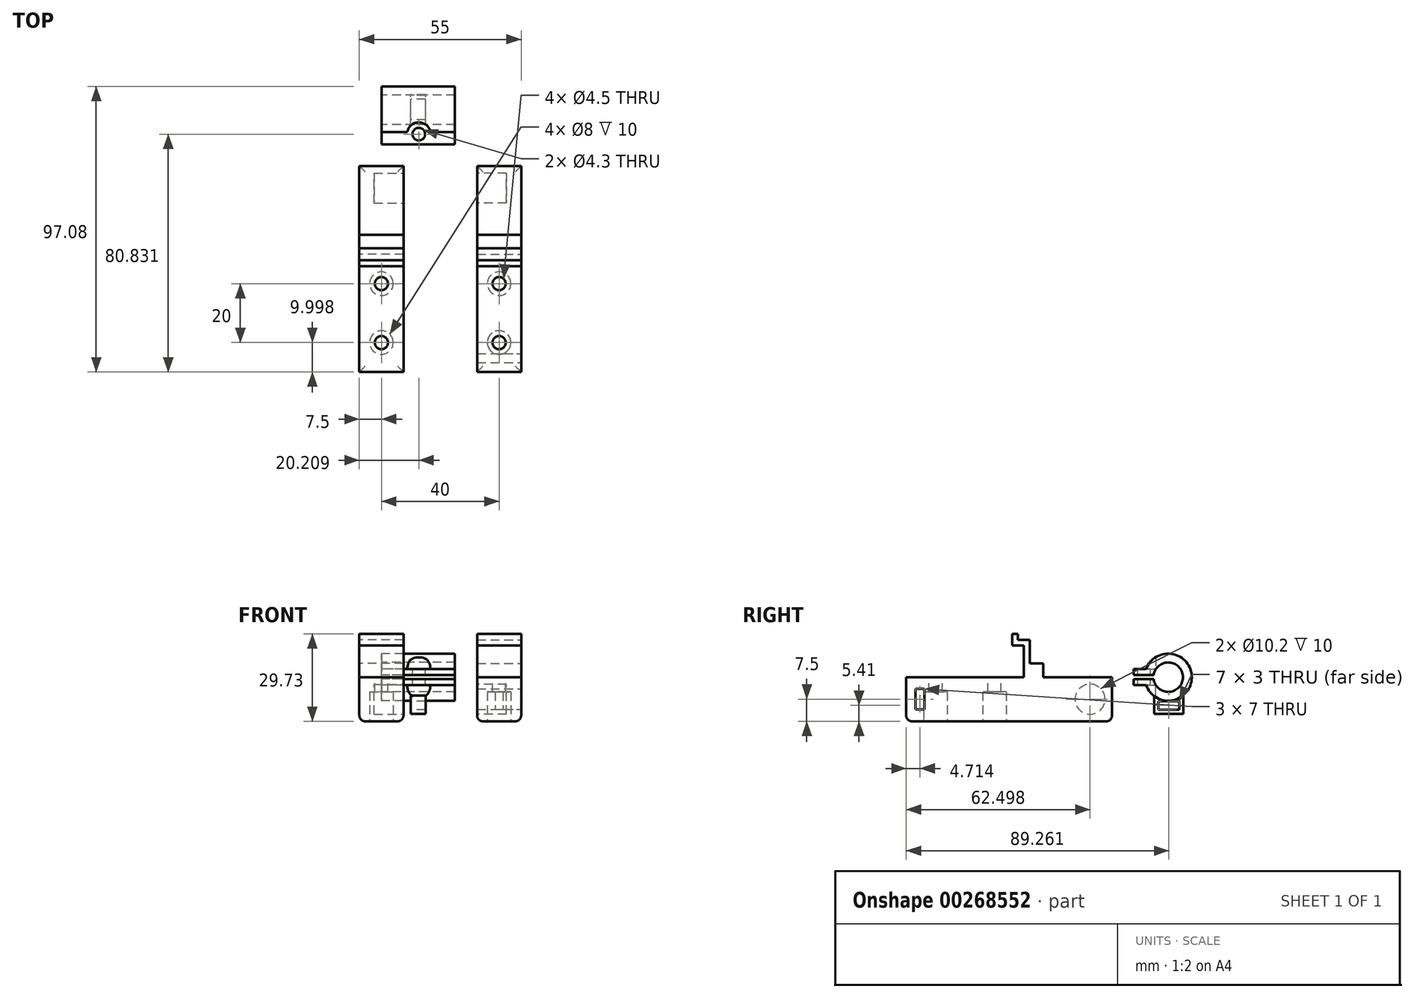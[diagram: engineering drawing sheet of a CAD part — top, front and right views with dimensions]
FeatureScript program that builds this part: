
annotation { "Feature Type Name" : "Feature", "Feature Type Description" : "" }
export const myFeature = defineFeature(function(context is Context, id is Id, definition is map)
    precondition{}
    {
        {
            var Q0;
            Q0=qCreatedBy(makeId("Top.planeOp"),FACE);
            var sketch = newSketch(context, id + "F0", { "sketchPlane" : qUnion([Q0])});
            skLineSegment(sketch, "E0", {"start": v(120.64, 20) * mm, "end": v(-98.83, 20) * mm, "construction": true});
            skLineSegment(sketch, "E1", {"start": v(-113.57, -20) * mm, "end": v(119.85, -20) * mm, "construction": true});
            skLineSegment(sketch, "E2", {"start": v(-15.81, 35.6) * mm, "end": v(120.22, 35.6) * mm, "construction": true});
            skLineSegment(sketch, "E3", {"start": v(0, 0) * mm, "end": v(121.2, 0) * mm, "construction": true});
            skSolve(sketch);
        }
        {
            var Q0;
            Q0=qCreatedBy(makeId("Right.planeOp"),FACE);
            var sketch = newSketch(context, id + "F1", { "sketchPlane" : qUnion([Q0])});
            skLineSegment(sketch, "E4", {"start": v(13.49, 0) * mm, "end": v(-26.51, 0) * mm});
            skLineSegment(sketch, "E5", {"start": v(-26.51, 0) * mm, "end": v(-26.51, -15) * mm});
            skLineSegment(sketch, "E6", {"start": v(-26.51, -15) * mm, "end": v(18.49, -15) * mm});
            skLineSegment(sketch, "E7", {"start": v(13.49, 10.73) * mm, "end": v(13.49, 0) * mm});
            skLineSegment(sketch, "E8", {"start": v(43.49, -15) * mm, "end": v(43.49, 0) * mm});
            skLineSegment(sketch, "E9", {"start": v(43.49, 0) * mm, "end": v(20.14, 0) * mm});
            skLineSegment(sketch, "E10", {"start": v(13.49, 10.73) * mm, "end": v(9.49, 10.73) * mm});
            skLineSegment(sketch, "E11", {"start": v(9.49, 10.73) * mm, "end": v(9.49, 14.73) * mm});
            skLineSegment(sketch, "E12", {"start": v(9.49, 14.73) * mm, "end": v(11.49, 14.73) * mm});
            skLineSegment(sketch, "E13", {"start": v(11.49, 14.73) * mm, "end": v(11.49, 12.73) * mm});
            skLineSegment(sketch, "E14", {"start": v(18.49, -15) * mm, "end": v(43.49, -15) * mm});
            skLineSegment(sketch, "E15", {"start": v(20.14, 0) * mm, "end": v(20.14, 4.7) * mm});
            skLineSegment(sketch, "E16", {"start": v(20.14, 4.7) * mm, "end": v(15.49, 4.7) * mm});
            skPoint(sketch, "E17.orphan", {"position": v(15.49, 0) * mm});
            skPoint(sketch, "E18.end.orphan", {"position": v(13.49, 21.47) * mm});
            skLineSegment(sketch, "E19", {"start": v(15.49, 4.7) * mm, "end": v(15.49, 12.7) * mm});
            skPoint(sketch, "E20.end.orphan", {"position": v(13.49, 12) * mm});
            skLineSegment(sketch, "E21", {"start": v(15.49, 12.7) * mm, "end": v(11.49, 12.73) * mm});
            skSolve(sketch);
        }
        {
            var Q0;
            Q0=makeQuery(id+"F1.imprint","IMPRINT",FACE,{"disambiguationData":[TD([[makeQuery(id+"F1.imprint","IMPRINT",EDGE,{"derivedFrom":sQuery(id+"F1.wireOp",EDGE,"E4")}),1.0]])]});
            var Q1;
            {var subQ0=sQuery(id+"F1.wireOp",EDGE,"E10");Q1=makeQuery(id+"F1.imprint","IMPRINT",FACE,{"disambiguationData":[TD([[makeQuery(id+"F1.imprint","IMPRINT",EDGE,{"derivedFrom":subQ0}),-1.0]])]});}
            extrude(context, id + "F2", {"entities" : qUnion([Q0, Q1]), "endBound" : BoundingType.SYMMETRIC, "depth" : 15 * mm});
        }
        {
            var Q0;
            Q0=makeQuery(id+"F2.opExtrude","CAP_FACE",FACE,{"disambiguationData":[OSD([sQuery(id+"F1.wireOp",EDGE,"E4"),sQuery(id+"F1.wireOp",EDGE,"E5"),sQuery(id+"F1.wireOp",EDGE,"E6"),sQuery(id+"F1.wireOp",EDGE,"E7"),sQuery(id+"F1.wireOp",EDGE,"E8"),sQuery(id+"F1.wireOp",EDGE,"E9"),sQuery(id+"F1.wireOp",EDGE,"E10"),sQuery(id+"F1.wireOp",EDGE,"E11"),sQuery(id+"F1.wireOp",EDGE,"E12"),sQuery(id+"F1.wireOp",EDGE,"E13"),sQuery(id+"F1.wireOp",EDGE,"E14"),sQuery(id+"F1.wireOp",EDGE,"E15"),sQuery(id+"F1.wireOp",EDGE,"E16"),sQuery(id+"F1.wireOp",EDGE,"E19"),sQuery(id+"F1.wireOp",EDGE,"E21")])],"isStart":false});
            var sketch = newSketch(context, id + "F3", { "sketchPlane" : qUnion([Q0])});
            skCircle(sketch, "E22", {"center": v(35.99, -7.5) * mm, "radius": 5.1 * mm});
            skSolve(sketch);
        }
        {
            var Q0;
            Q0=makeQuery(id+"F3.imprint","IMPRINT",FACE,{"disambiguationData":[TD([[makeQuery(id+"F3.imprint","IMPRINT",EDGE,{"derivedFrom":sQuery(id+"F3.wireOp",EDGE,"E22")}),1.0]])]});
            extrude(context, id + "F4", {"entities" : qUnion([Q0]), "operationType" : NewBodyOperationType.REMOVE, "oppositeDirection" : true, "depth" : 10 * mm});
        }
        {
            var Q0;
            Q0=qCreatedBy(makeId("Right.planeOp"),FACE);
            cPlane(context, id + "F5", {"entities" : qUnion([Q0]), "cplaneType" : CPlaneType.OFFSET, "offset" : 20 * mm, "width" : 150 * mm, "height" : 150 * mm});
        }
        {
            var Q0;
            Q0=makeQuery(id+"F2.opExtrude","SWEPT_BODY",BODY,{"disambiguationData":[OSD([sQuery(id+"F1.wireOp",EDGE,"E4"),sQuery(id+"F1.wireOp",EDGE,"E5"),sQuery(id+"F1.wireOp",EDGE,"E6"),sQuery(id+"F1.wireOp",EDGE,"E7"),sQuery(id+"F1.wireOp",EDGE,"E8"),sQuery(id+"F1.wireOp",EDGE,"E9"),sQuery(id+"F1.wireOp",EDGE,"E10"),sQuery(id+"F1.wireOp",EDGE,"E11"),sQuery(id+"F1.wireOp",EDGE,"E12"),sQuery(id+"F1.wireOp",EDGE,"E13"),sQuery(id+"F1.wireOp",EDGE,"E14"),sQuery(id+"F1.wireOp",EDGE,"E15"),sQuery(id+"F1.wireOp",EDGE,"E16"),sQuery(id+"F1.wireOp",EDGE,"E19"),sQuery(id+"F1.wireOp",EDGE,"E21")])]});
            var Q1;
            Q1=qCreatedBy(id+"F5.planeOp",FACE);
            mirror(context, id + "F6", {"entities" : qUnion([Q0]), "mirrorPlane" : qUnion([Q1])});
        }
        {
            var Q0;
            Q0=makeQuery(id+"F6.opPattern","COPY",FACE,{"derivedFrom":makeQuery(id+"F2.opExtrude","CAP_FACE",FACE,{"disambiguationData":[OSD([sQuery(id+"F1.wireOp",EDGE,"E4"),sQuery(id+"F1.wireOp",EDGE,"E5"),sQuery(id+"F1.wireOp",EDGE,"E6"),sQuery(id+"F1.wireOp",EDGE,"E7"),sQuery(id+"F1.wireOp",EDGE,"E8"),sQuery(id+"F1.wireOp",EDGE,"E9"),sQuery(id+"F1.wireOp",EDGE,"E10"),sQuery(id+"F1.wireOp",EDGE,"E11"),sQuery(id+"F1.wireOp",EDGE,"E12"),sQuery(id+"F1.wireOp",EDGE,"E13"),sQuery(id+"F1.wireOp",EDGE,"E14"),sQuery(id+"F1.wireOp",EDGE,"E15"),sQuery(id+"F1.wireOp",EDGE,"E16"),sQuery(id+"F1.wireOp",EDGE,"E19"),sQuery(id+"F1.wireOp",EDGE,"E21")])],"isStart":true}),"instanceName":"1"});
            var sketch = newSketch(context, id + "F7", { "sketchPlane" : qUnion([Q0])});
            skLineSegment(sketch, "E23.bottom", {"start": v(-20.3, -4) * mm, "end": v(-23.3, -4) * mm});
            skLineSegment(sketch, "E23.top", {"start": v(-20.3, -11) * mm, "end": v(-23.3, -11) * mm});
            skLineSegment(sketch, "E23.left", {"start": v(-20.3, -4) * mm, "end": v(-20.3, -11) * mm});
            skLineSegment(sketch, "E23.right", {"start": v(-23.3, -4) * mm, "end": v(-23.3, -11) * mm});
            skSolve(sketch);
        }
        {
            var Q0;
            Q0=makeQuery(id+"F7.imprint","IMPRINT",FACE,{"disambiguationData":[TD([[makeQuery(id+"F7.imprint","IMPRINT",EDGE,{"derivedFrom":sQuery(id+"F7.wireOp",EDGE,"E23.bottom")}),1.0]])]});
            extrude(context, id + "F8", {"entities" : qUnion([Q0]), "operationType" : NewBodyOperationType.REMOVE, "endBound" : BoundingType.UP_TO_NEXT, "oppositeDirection" : true, "depth" : 25 * mm});
        }
        {
            var Q0;
            Q0=makeQuery(id+"F8.boolean.opBoolean","COPY",EDGE,{"derivedFrom":makeQuery(id+"F8.opExtrude","CAP_EDGE",EDGE,{"disambiguationData":[OSD([sQuery(id+"F7.wireOp",EDGE,"E23.right")])],"isStart":true})});
            var Q1;
            Q1=makeQuery(id+"F8.boolean.opBoolean","COPY",EDGE,{"derivedFrom":makeQuery(id+"F8.opExtrude","TWEAK_EDGE",EDGE,{"derivedFrom":[makeQuery(id+"F6.opPattern","COPY",FACE,{"derivedFrom":makeQuery(id+"F2.opExtrude","CAP_FACE",FACE,{"disambiguationData":[OSD([sQuery(id+"F1.wireOp",EDGE,"E4"),sQuery(id+"F1.wireOp",EDGE,"E5"),sQuery(id+"F1.wireOp",EDGE,"E6"),sQuery(id+"F1.wireOp",EDGE,"E7"),sQuery(id+"F1.wireOp",EDGE,"E8"),sQuery(id+"F1.wireOp",EDGE,"E9"),sQuery(id+"F1.wireOp",EDGE,"E10"),sQuery(id+"F1.wireOp",EDGE,"E11"),sQuery(id+"F1.wireOp",EDGE,"E12"),sQuery(id+"F1.wireOp",EDGE,"E13"),sQuery(id+"F1.wireOp",EDGE,"E14"),sQuery(id+"F1.wireOp",EDGE,"E15"),sQuery(id+"F1.wireOp",EDGE,"E16"),sQuery(id+"F1.wireOp",EDGE,"E19"),sQuery(id+"F1.wireOp",EDGE,"E21")])],"isStart":false}),"instanceName":"1"}),makeQuery(id+"F7.imprint","IMPRINT",EDGE,{"derivedFrom":sQuery(id+"F7.wireOp",EDGE,"E23.right")})]})});
            var Q2;
            Q2=makeQuery(id+"F6.opPattern","COPY",EDGE,{"derivedFrom":makeQuery(id+"F2.opExtrude","CAP_EDGE",EDGE,{"disambiguationData":[OSD([sQuery(id+"F1.wireOp",EDGE,"E6"),sQuery(id+"F1.wireOp",EDGE,"E14")])],"isStart":false}),"instanceName":"1"});
            var Q3;
            Q3=makeQuery(id+"F6.opPattern","COPY",EDGE,{"derivedFrom":makeQuery(id+"F2.opExtrude","CAP_EDGE",EDGE,{"disambiguationData":[OSD([sQuery(id+"F1.wireOp",EDGE,"E6"),sQuery(id+"F1.wireOp",EDGE,"E14")])],"isStart":true}),"instanceName":"1"});
            var Q4;
            Q4=makeQuery(id+"F2.opExtrude","CAP_EDGE",EDGE,{"disambiguationData":[OSD([sQuery(id+"F1.wireOp",EDGE,"E6"),sQuery(id+"F1.wireOp",EDGE,"E14")])],"isStart":true});
            var Q5;
            Q5=makeQuery(id+"F2.opExtrude","CAP_EDGE",EDGE,{"disambiguationData":[OSD([sQuery(id+"F1.wireOp",EDGE,"E6"),sQuery(id+"F1.wireOp",EDGE,"E14")])],"isStart":false});
            var Q6;
            Q6=makeQuery(id+"F6.opPattern","COPY",EDGE,{"derivedFrom":makeQuery(id+"F2.opExtrude","SWEPT_EDGE",EDGE,{"disambiguationData":[OSD([sQuery(id+"F1.wireOp",EDGE,"E5"),sQuery(id+"F1.wireOp",EDGE,"E6")])]}),"instanceName":"1"});
            var Q7;
            Q7=makeQuery(id+"F2.opExtrude","SWEPT_EDGE",EDGE,{"disambiguationData":[OSD([sQuery(id+"F1.wireOp",EDGE,"E5"),sQuery(id+"F1.wireOp",EDGE,"E6")])]});
            var Q8;
            Q8=makeQuery(id+"F2.opExtrude","SWEPT_EDGE",EDGE,{"disambiguationData":[OSD([sQuery(id+"F1.wireOp",EDGE,"E8"),sQuery(id+"F1.wireOp",EDGE,"E14")])]});
            var Q9;
            Q9=makeQuery(id+"F6.opPattern","COPY",EDGE,{"derivedFrom":makeQuery(id+"F2.opExtrude","SWEPT_EDGE",EDGE,{"disambiguationData":[OSD([sQuery(id+"F1.wireOp",EDGE,"E8"),sQuery(id+"F1.wireOp",EDGE,"E14")])]}),"instanceName":"1"});
            fillet(context, id + "F9", {"entities" : qUnion([Q0, Q1, Q2, Q3, Q4, Q5, Q6, Q7, Q8, Q9]), "radius" : 2 * mm, "tangentPropagation" : true, "allowEdgeOverflow" : false});
        }
        {
            var Q0;
            Q0=makeQuery(id+"F2.opExtrude","SWEPT_FACE",FACE,{"disambiguationData":[OSD([sQuery(id+"F1.wireOp",EDGE,"E4")])]});
            var sketch = newSketch(context, id + "F10", { "sketchPlane" : qUnion([Q0])});
            skCircle(sketch, "E24", {"center": v(0, 3.49) * mm, "radius": 2.25 * mm});
            skCircle(sketch, "E25", {"center": v(0, -16.51) * mm, "radius": 2.25 * mm});
            skSolve(sketch);
        }
        {
            var Q0;
            Q0=makeQuery(id+"F10.imprint","IMPRINT",FACE,{"disambiguationData":[TD([[makeQuery(id+"F10.imprint","IMPRINT",EDGE,{"derivedFrom":sQuery(id+"F10.wireOp",EDGE,"E24")}),1.0]])]});
            var Q1;
            Q1=makeQuery(id+"F10.imprint","IMPRINT",FACE,{"disambiguationData":[TD([[makeQuery(id+"F10.imprint","IMPRINT",EDGE,{"derivedFrom":sQuery(id+"F10.wireOp",EDGE,"E25")}),1.0]])]});
            var Q2;
            Q2=sQuery(id+"F10.wireOp",EDGE,"E24");
            var Q3;
            Q3=sQuery(id+"F10.wireOp",EDGE,"E25");
            extrude(context, id + "F11", {"entities" : qUnion([Q0, Q1]), "operationType" : NewBodyOperationType.REMOVE, "surfaceEntities" : qUnion([Q2, Q3]), "endBound" : BoundingType.UP_TO_NEXT, "oppositeDirection" : true, "depth" : 25 * mm});
        }
        {
            var Q0;
            Q0=makeQuery(id+"F6.opPattern","COPY",FACE,{"derivedFrom":makeQuery(id+"F2.opExtrude","SWEPT_FACE",FACE,{"disambiguationData":[OSD([sQuery(id+"F1.wireOp",EDGE,"E4")])]}),"instanceName":"1"});
            var sketch = newSketch(context, id + "F12", { "sketchPlane" : qUnion([Q0])});
            skCircle(sketch, "E26", {"center": v(40, 3.49) * mm, "radius": 2.25 * mm});
            skCircle(sketch, "E27", {"center": v(40, -16.51) * mm, "radius": 2.25 * mm});
            skSolve(sketch);
        }
        {
            var Q0;
            Q0=makeQuery(id+"F12.imprint","IMPRINT",FACE,{"disambiguationData":[TD([[makeQuery(id+"F12.imprint","IMPRINT",EDGE,{"derivedFrom":sQuery(id+"F12.wireOp",EDGE,"E26")}),1.0]])]});
            var Q1;
            Q1=makeQuery(id+"F12.imprint","IMPRINT",FACE,{"disambiguationData":[TD([[makeQuery(id+"F12.imprint","IMPRINT",EDGE,{"derivedFrom":sQuery(id+"F12.wireOp",EDGE,"E27")}),1.0]])]});
            extrude(context, id + "F13", {"entities" : qUnion([Q0, Q1]), "operationType" : NewBodyOperationType.REMOVE, "endBound" : BoundingType.UP_TO_NEXT, "oppositeDirection" : true, "depth" : 25 * mm});
        }
        {
            var Q0;
            Q0=makeQuery(id+"F6.opPattern","COPY",FACE,{"derivedFrom":makeQuery(id+"F2.opExtrude","SWEPT_FACE",FACE,{"disambiguationData":[OSD([sQuery(id+"F1.wireOp",EDGE,"E6"),sQuery(id+"F1.wireOp",EDGE,"E14")])]}),"instanceName":"1"});
            var sketch = newSketch(context, id + "F14", { "sketchPlane" : qUnion([Q0])});
            skCircle(sketch, "E28", {"center": v(40, -3.49) * mm, "radius": 4 * mm});
            skCircle(sketch, "E29", {"center": v(40, 16.51) * mm, "radius": 4 * mm});
            skSolve(sketch);
        }
        {
            var Q0;
            Q0=makeQuery(id+"F14.imprint","IMPRINT",FACE,{"disambiguationData":[TD([[makeQuery(id+"F14.imprint","IMPRINT",EDGE,{"derivedFrom":sQuery(id+"F14.wireOp",EDGE,"E28")}),1.0]])]});
            var Q1;
            Q1=makeQuery(id+"F14.imprint","IMPRINT",FACE,{"disambiguationData":[TD([[makeQuery(id+"F14.imprint","IMPRINT",EDGE,{"derivedFrom":sQuery(id+"F14.wireOp",EDGE,"E29")}),1.0]])]});
            extrude(context, id + "F15", {"entities" : qUnion([Q0, Q1]), "operationType" : NewBodyOperationType.REMOVE, "oppositeDirection" : true, "depth" : 10 * mm});
        }
        {
            var Q0;
            Q0=makeQuery(id+"F2.opExtrude","SWEPT_FACE",FACE,{"disambiguationData":[OSD([sQuery(id+"F1.wireOp",EDGE,"E6"),sQuery(id+"F1.wireOp",EDGE,"E14")])]});
            var sketch = newSketch(context, id + "F16", { "sketchPlane" : qUnion([Q0])});
            skCircle(sketch, "E30", {"center": v(0, -3.49) * mm, "radius": 4 * mm});
            skCircle(sketch, "E31", {"center": v(0, 16.51) * mm, "radius": 4 * mm});
            skSolve(sketch);
        }
        {
            var Q0;
            Q0=makeQuery(id+"F16.imprint","IMPRINT",FACE,{"disambiguationData":[TD([[makeQuery(id+"F16.imprint","IMPRINT",EDGE,{"derivedFrom":sQuery(id+"F16.wireOp",EDGE,"E30")}),1.0]])]});
            var Q1;
            Q1=makeQuery(id+"F16.imprint","IMPRINT",FACE,{"disambiguationData":[TD([[makeQuery(id+"F16.imprint","IMPRINT",EDGE,{"derivedFrom":sQuery(id+"F16.wireOp",EDGE,"E31")}),1.0]])]});
            extrude(context, id + "F17", {"entities" : qUnion([Q0, Q1]), "operationType" : NewBodyOperationType.REMOVE, "oppositeDirection" : true, "depth" : 10 * mm});
        }
        {
            var Q0;
            Q0=qCreatedBy(makeId("Right.planeOp"),FACE);
            var sketch = newSketch(context, id + "F18", { "sketchPlane" : qUnion([Q0])});
            skArc(sketch, "E32", {"start": v(57.63, -0.71) * mm, "mid": v(67.57, 0) * mm, "end": v(57.63, 0.71) * mm});
            skArc(sketch, "E33", {"start": v(55.05, -2.71) * mm, "mid": v(70.57, 0) * mm, "end": v(55.05, 2.71) * mm});
            skLineSegment(sketch, "E34", {"start": v(57.63, -0.71) * mm, "end": v(54.6, -0.71) * mm});
            skLineSegment(sketch, "E35.MirrorCS", {"start": v(57.63, 0.71) * mm, "end": v(54.6, 0.71) * mm});
            skLineSegment(sketch, "E36.bottom", {"start": v(57.63, 0.71) * mm, "end": v(50.84, 0.71) * mm});
            skLineSegment(sketch, "E36.top", {"start": v(55.05, 2.71) * mm, "end": v(50.84, 2.71) * mm});
            skLineSegment(sketch, "E36.right", {"start": v(50.84, 0.71) * mm, "end": v(50.84, 2.71) * mm});
            skLineSegment(sketch, "E37.MirrorCS", {"start": v(55.05, -2.71) * mm, "end": v(50.84, -2.71) * mm});
            skLineSegment(sketch, "E38.MirrorCS", {"start": v(50.84, -0.71) * mm, "end": v(50.84, -2.71) * mm});
            skLineSegment(sketch, "E39.MirrorCS", {"start": v(57.63, -0.71) * mm, "end": v(50.84, -0.71) * mm});
            skPoint(sketch, "E40.orphan", {"position": v(57.63, -2.71) * mm});
            skPoint(sketch, "E41.MirrorCS.start.orphan", {"position": v(57.63, -0.71) * mm});
            skPoint(sketch, "E36.left.end.orphan", {"position": v(57.63, 2.71) * mm});
            skSolve(sketch);
        }
        {
            var Q0;
            {var subQ3=sQuery(id+"F18.wireOp",EDGE,"E32");Q0=makeQuery(id+"F18.imprint","IMPRINT",FACE,{"disambiguationData":[TD([[makeQuery(id+"F18.imprint","IMPRINT",EDGE,{"derivedFrom":subQ3}),-1.0]])]});}
            extrude(context, id + "F19", {"entities" : qUnion([Q0]), "depth" : 25 * mm});
        }
        {
            var Q0;
            Q0=qCreatedBy(makeId("Top.planeOp"),FACE);
            var sketch = newSketch(context, id + "F20", { "sketchPlane" : qUnion([Q0])});
            skCircle(sketch, "E42", {"center": v(12.7, 54.32) * mm, "radius": 2.15 * mm});
            skSolve(sketch);
        }
        {
            var Q0;
            Q0 = qSketchRegion(id + "F20", true);
            var Q1;
            Q1=sQuery(id+"F20.wireOp",EDGE,"E42");
            extrude(context, id + "F21", {"entities" : qUnion([Q0]), "operationType" : NewBodyOperationType.REMOVE, "surfaceEntities" : qUnion([Q1]), "endBound" : BoundingType.SYMMETRIC, "oppositeDirection" : true, "depth" : 25 * mm});
        }
        {
            var Q0;
            Q0=makeQuery(id+"F19.opExtrude","SWEPT_FACE",FACE,{"disambiguationData":[OSD([sQuery(id+"F18.wireOp",EDGE,"E37.MirrorCS")])]});
            var sketch = newSketch(context, id + "F22", { "sketchPlane" : qUnion([Q0])});
            skCircle(sketch, "E43", {"center": v(12.7, -54.32) * mm, "radius": 4 * mm});
            skSolve(sketch);
        }
        {
            var Q0;
            Q0 = qSketchRegion(id + "F22", true);
            extrude(context, id + "F23", {"entities" : qUnion([Q0]), "operationType" : NewBodyOperationType.REMOVE, "depth" : 25 * mm});
        }
        {
            var Q0;
            Q0=makeQuery(id+"F19.opExtrude","SWEPT_FACE",FACE,{"disambiguationData":[OSD([sQuery(id+"F18.wireOp",EDGE,"E36.top")])]});
            var sketch = newSketch(context, id + "F24", { "sketchPlane" : qUnion([Q0])});
            skCircle(sketch, "E44", {"center": v(12.7, 54.32) * mm, "radius": 4 * mm});
            skSolve(sketch);
        }
        {
            var Q0;
            Q0 = qSketchRegion(id + "F24", true);
            extrude(context, id + "F25", {"entities" : qUnion([Q0]), "operationType" : NewBodyOperationType.REMOVE, "depth" : 25 * mm});
        }
        {
            var Q0;
            Q0=qCreatedBy(makeId("Right.planeOp"),FACE);
            cPlane(context, id + "F26", {"entities" : qUnion([Q0]), "cplaneType" : CPlaneType.OFFSET, "offset" : 12.5 * mm, "width" : 150 * mm, "height" : 150 * mm});
        }
        {
            var Q0;
            Q0=qCreatedBy(id+"F26.planeOp",FACE);
            var sketch = newSketch(context, id + "F27", { "sketchPlane" : qUnion([Q0])});
            skLineSegment(sketch, "E45.bottom", {"start": v(57.76, -6.3) * mm, "end": v(57.75, -12.5) * mm});
            skLineSegment(sketch, "E45.left", {"start": v(57.76, -6.3) * mm, "end": v(62.76, -6.3) * mm});
            skLineSegment(sketch, "E46.MirrorCS", {"start": v(67.76, -6.3) * mm, "end": v(67.76, -12.5) * mm});
            skLineSegment(sketch, "E47.MirrorCS", {"start": v(67.76, -6.3) * mm, "end": v(62.76, -6.3) * mm});
            skLineSegment(sketch, "E48", {"start": v(57.75, -12.5) * mm, "end": v(67.76, -12.5) * mm});
            skLineSegment(sketch, "E49.bottom", {"start": v(59.25, -11.09) * mm, "end": v(59.25, -8.09) * mm});
            skLineSegment(sketch, "E49.top", {"start": v(66.25, -11.09) * mm, "end": v(66.25, -8.09) * mm});
            skLineSegment(sketch, "E49.left", {"start": v(59.25, -11.09) * mm, "end": v(66.25, -11.09) * mm});
            skLineSegment(sketch, "E49.right", {"start": v(59.25, -8.09) * mm, "end": v(66.25, -8.09) * mm});
            skSolve(sketch);
        }
        {
            var Q0;
            Q0 = qSketchRegion(id + "F27", true);
            extrude(context, id + "F28", {"entities" : qUnion([Q0]), "operationType" : NewBodyOperationType.ADD, "endBound" : BoundingType.SYMMETRIC, "depth" : 5 * mm});
        }
    });
